# Revit family: E-771
name_source: partatom
category: Plumbing Fixtures
revit_build: Autodesk Revit 2014 (Build: 20130308_1515(x64)
units: mm (PartAtom-declared; Revit-internal decimal feet)

## types (1)
- E-771
    Brass Chromed = Brass Chromed
    CW Connection = Yes
    Description = Nuva Pressure Balance Valve With Volume Control With Diverter
    Documentation = http://www.helvex.com.mx
    Features = Ceramic Cartridge
    HW Connection = Yes
    Height Shower = 47"
    Height Tub = 33"
    Inlet Threads = 1/2" 14 NPT Shower and 3/4" 14 NPT Tub
    Manufacturer = Helvex
    Max. Working Pressure = 85.3 psi
    Min. Working Pressure = 17.1 psi
    Model = E-771
    Niquel Duravex = Niquel Duravex
    Satin = Satin
    Shower Valve Installation Depth Range = 0.5" (12.7 mm) Max.
    Type Comments = Shower and/or Tube Single Control Faucets
    URL = http://www.helvex.com.mx

## geometry (parser evidence)
native form markers: Sweep x1
no freeform markers — native parametric forms only
